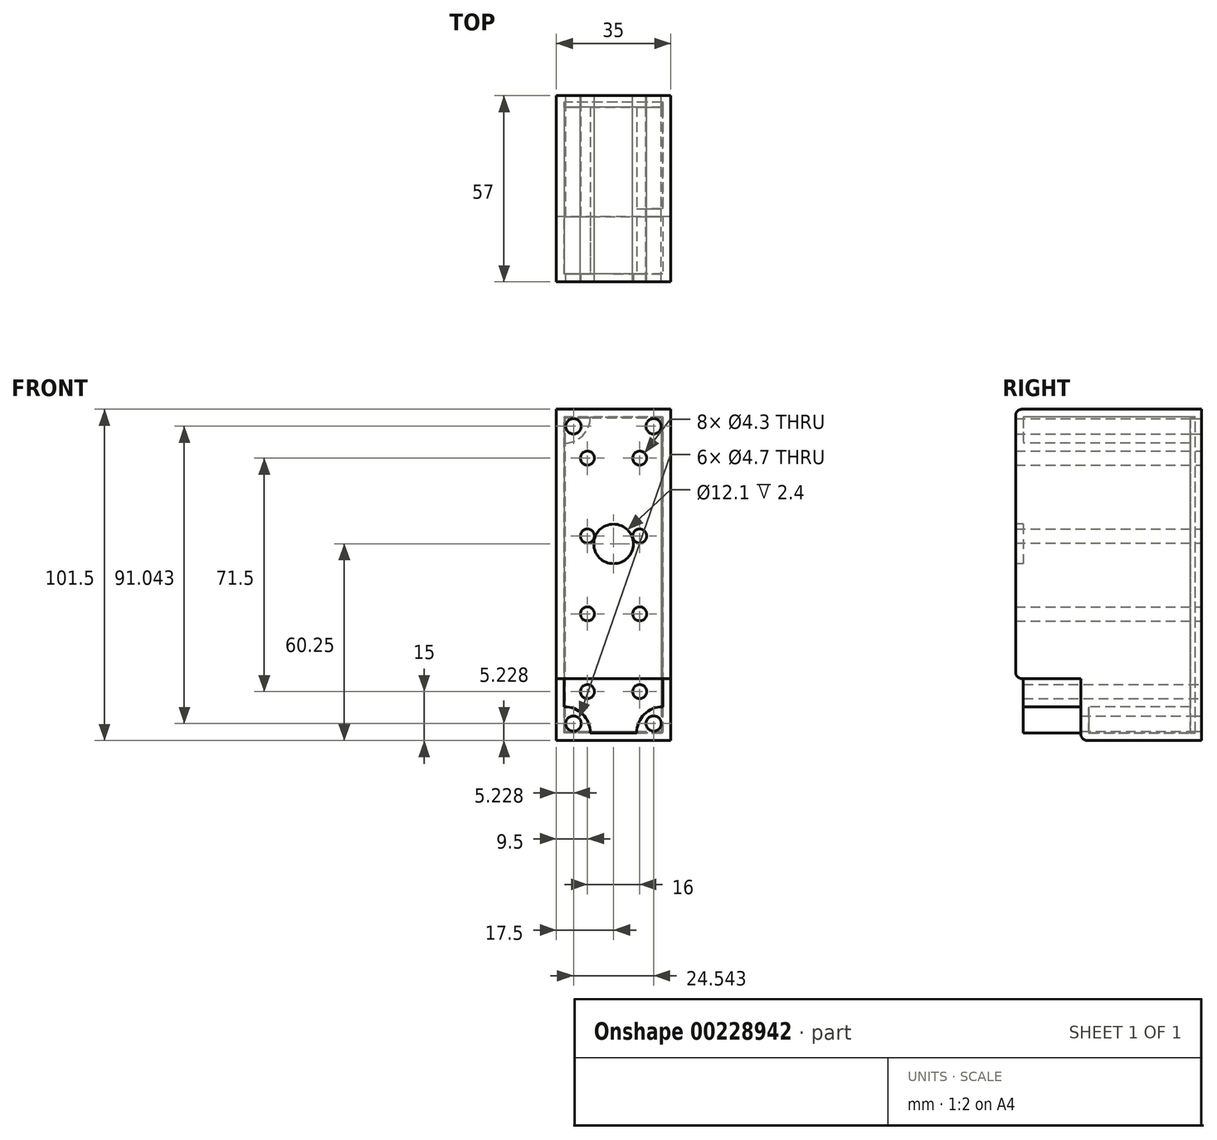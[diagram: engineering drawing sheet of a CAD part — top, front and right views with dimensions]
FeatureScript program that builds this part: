
annotation { "Feature Type Name" : "Feature", "Feature Type Description" : "" }
export const myFeature = defineFeature(function(context is Context, id is Id, definition is map)
    precondition{}
    {
        {
            var Q0;
            Q0=qCreatedBy(makeId("Right.planeOp"),FACE);
            var sketch = newSketch(context, id + "F0", { "sketchPlane" : qUnion([Q0])});
            skLineSegment(sketch, "E0", {"start": v(20, 0) * mm, "end": v(55, 0) * mm});
            skLineSegment(sketch, "E1", {"start": v(55, 0) * mm, "end": v(55, 101.5) * mm});
            skLineSegment(sketch, "E2", {"start": v(55, 101.5) * mm, "end": v(0, 101.5) * mm});
            skLineSegment(sketch, "E3", {"start": v(0, 101.5) * mm, "end": v(0, 19) * mm});
            skLineSegment(sketch, "E4", {"start": v(0, 19) * mm, "end": v(20, 19) * mm});
            skLineSegment(sketch, "E5", {"start": v(20, 19) * mm, "end": v(20, 0) * mm});
            skSolve(sketch);
        }
        {
            var Q0;
            Q0=makeQuery(id+"F0.imprint","IMPRINT",FACE,{"disambiguationData":[TD([[makeQuery(id+"F0.imprint","IMPRINT",EDGE,{"derivedFrom":sQuery(id+"F0.wireOp",EDGE,"E0")}),1.0]])]});
            extrude(context, id + "F1", {"entities" : qUnion([Q0]), "depth" : 35 * mm});
        }
        {
            var Q0;
            Q0=makeQuery(id+"F1.opExtrude","SWEPT_EDGE",EDGE,{"disambiguationData":[OSD([sQuery(id+"F0.wireOp",EDGE,"E2"),sQuery(id+"F0.wireOp",EDGE,"E3")])]});
            var Q1;
            Q1=makeQuery(id+"F1.opExtrude","SWEPT_EDGE",EDGE,{"disambiguationData":[OSD([sQuery(id+"F0.wireOp",EDGE,"E3"),sQuery(id+"F0.wireOp",EDGE,"E4")])]});
            var Q2;
            Q2=makeQuery(id+"F1.opExtrude","SWEPT_EDGE",EDGE,{"disambiguationData":[OSD([sQuery(id+"F0.wireOp",EDGE,"E0"),sQuery(id+"F0.wireOp",EDGE,"E5")])]});
            fillet(context, id + "F2", {"entities" : qUnion([Q0, Q1, Q2]), "radius" : 2 * mm, "tangentPropagation" : true, "allowEdgeOverflow" : false});
        }
        {
            var Q0;
            Q0=makeQuery(id+"F1.opExtrude","SWEPT_FACE",FACE,{"disambiguationData":[OSD([sQuery(id+"F0.wireOp",EDGE,"E1")])]});
            shell(context, id + "F3", {"entities" : qUnion([Q0]), "thickness" : 2.4 * mm});
        }
        {
            var Q0;
            Q0=makeQuery(id+"F1.opExtrude","SWEPT_FACE",FACE,{"disambiguationData":[OSD([sQuery(id+"F0.wireOp",EDGE,"E3")])]});
            var sketch = newSketch(context, id + "F4", { "sketchPlane" : qUnion([Q0])});
            skPoint(sketch, "E6.0", {"position": v(0, 101.5) * mm});
            skPoint(sketch, "E7.0", {"position": v(35, 19) * mm});
            skLineSegment(sketch, "E8", {"start": v(0, 101.5) * mm, "end": v(35, 19) * mm, "construction": true});
            skCircle(sketch, "E9", {"center": v(17.5, 60.25) * mm, "radius": 6.05 * mm});
            skSolve(sketch);
        }
        {
            var Q0;
            Q0=makeQuery(id+"F4.imprint","IMPRINT",FACE,{"disambiguationData":[TD([[makeQuery(id+"F4.imprint","IMPRINT",EDGE,{"derivedFrom":sQuery(id+"F4.wireOp",EDGE,"E9")}),1.0]])]});
            extrude(context, id + "F5", {"entities" : qUnion([Q0]), "operationType" : NewBodyOperationType.REMOVE, "endBound" : BoundingType.THROUGH_ALL, "oppositeDirection" : true, "depth" : 25 * mm});
        }
        {
            var Q0;
            Q0=makeQuery(id+"F1.opExtrude","SWEPT_FACE",FACE,{"disambiguationData":[OSD([sQuery(id+"F0.wireOp",EDGE,"E1")])]});
            var sketch = newSketch(context, id + "F6", { "sketchPlane" : qUnion([Q0])});
            skLineSegment(sketch, "E10.0", {"start": v(-35, 101.5) * mm, "end": v(0, 101.5) * mm});
            skLineSegment(sketch, "E11.0", {"start": v(-35, 0) * mm, "end": v(-35, 101.5) * mm});
            skLineSegment(sketch, "E12.0", {"start": v(-35, 0) * mm, "end": v(0, 0) * mm});
            skLineSegment(sketch, "E13.0", {"start": v(0, 0) * mm, "end": v(0, 101.5) * mm});
            skLineSegment(sketch, "E14.0", {"start": v(-32.25, 98.75) * mm, "end": v(-2.75, 98.75) * mm});
            skLineSegment(sketch, "E14.1", {"start": v(-32.25, 2.75) * mm, "end": v(-32.25, 98.75) * mm});
            skLineSegment(sketch, "E14.2", {"start": v(-32.25, 2.75) * mm, "end": v(-2.75, 2.75) * mm});
            skLineSegment(sketch, "E14.3", {"start": v(-2.75, 2.75) * mm, "end": v(-2.75, 98.75) * mm});
            skSolve(sketch);
        }
        {
            var Q0;
            Q0=makeQuery(id+"F6.imprint","IMPRINT",FACE,{"disambiguationData":[TD([[makeQuery(id+"F6.imprint","IMPRINT",EDGE,{"derivedFrom":sQuery(id+"F6.wireOp",EDGE,"E14.0")}),-1.0]])]});
            extrude(context, id + "F7", {"entities" : qUnion([Q0]), "oppositeDirection" : true, "depth" : 1.5 * mm});
        }
        {
            var Q0;
            Q0=makeQuery(id+"F6.imprint","IMPRINT",FACE,{"disambiguationData":[TD([[makeQuery(id+"F6.imprint","IMPRINT",EDGE,{"derivedFrom":sQuery(id+"F6.wireOp",EDGE,"E10.0")}),-1.0]])]});
            var Q1;
            Q1=makeQuery(id+"F6.imprint","IMPRINT",FACE,{"disambiguationData":[TD([[makeQuery(id+"F6.imprint","IMPRINT",EDGE,{"derivedFrom":sQuery(id+"F6.wireOp",EDGE,"E14.0")}),-1.0]])]});
            var Q2;
            Q2=makeQuery(id+"F6.imprint","IMPRINT",FACE,{"disambiguationData":[TD([[makeQuery(id+"F6.imprint","IMPRINT",EDGE,{"derivedFrom":sQuery(id+"F6.wireOp",EDGE,"E14.0")}),1.0]])]});
            extrude(context, id + "F8", {"entities" : qUnion([Q0, Q1, Q2]), "operationType" : NewBodyOperationType.ADD, "depth" : 2 * mm});
        }
        {
            var Q0;
            Q0=makeQuery(id+"F3.opShell","OFFSET_FACE",FACE,{"disambiguationData":[OSD([sQuery(id+"F0.wireOp",EDGE,"E3")])]});
            var sketch = newSketch(context, id + "F9", { "sketchPlane" : qUnion([Q0])});
            skLineSegment(sketch, "E15.0", {"start": v(-32.6, 99.1) * mm, "end": v(-2.4, 99.1) * mm});
            skLineSegment(sketch, "E16.0", {"start": v(-32.6, 2.4) * mm, "end": v(-32.6, 99.1) * mm});
            skLineSegment(sketch, "E17.0", {"start": v(-32.6, 2.4) * mm, "end": v(-2.4, 2.4) * mm});
            skLineSegment(sketch, "E18.0", {"start": v(-2.4, 2.4) * mm, "end": v(-2.4, 99.1) * mm});
            skArc(sketch, "E19", {"start": v(-32.6, 91.1) * mm, "mid": v(-26.94, 93.44) * mm, "end": v(-24.6, 99.1) * mm});
            skCircle(sketch, "E20", {"center": v(-29.77, 96.27) * mm, "radius": 1.75 * mm});
            skLineSegment(sketch, "E21", {"start": v(-32.6, 99.1) * mm, "end": v(-26.94, 93.44) * mm, "construction": true});
            skLineSegment(sketch, "E22", {"start": v(-17.5, 99.1) * mm, "end": v(-17.5, 2.4) * mm, "construction": true});
            skLineSegment(sketch, "E23", {"start": v(-32.6, 50.75) * mm, "end": v(-2.4, 50.75) * mm, "construction": true});
            skArc(sketch, "E24.MirrorCS", {"start": v(-2.4, 91.1) * mm, "mid": v(-8.06, 93.44) * mm, "end": v(-10.4, 99.1) * mm});
            skCircle(sketch, "E25.MirrorC", {"center": v(-5.23, 96.27) * mm, "radius": 1.75 * mm});
            skArc(sketch, "E26.MirrorCS", {"start": v(-32.6, 10.4) * mm, "mid": v(-26.94, 8.06) * mm, "end": v(-24.6, 2.4) * mm});
            skCircle(sketch, "E27.MirrorC", {"center": v(-29.77, 5.23) * mm, "radius": 1.75 * mm});
            skArc(sketch, "E28.MirrorCS", {"start": v(-2.4, 10.4) * mm, "mid": v(-8.06, 8.06) * mm, "end": v(-10.4, 2.4) * mm});
            skCircle(sketch, "E29.MirrorC", {"center": v(-5.23, 5.23) * mm, "radius": 1.75 * mm});
            skSolve(sketch);
        }
        {
            var Q0;
            {var subQ3=sQuery(id+"F9.wireOp",EDGE,"E24.MirrorCS");Q0=makeQuery(id+"F9.imprint","IMPRINT",FACE,{"disambiguationData":[TD([[makeQuery(id+"F9.imprint","IMPRINT",EDGE,{"derivedFrom":subQ3}),-1.0]])]});}
            var Q1;
            {var subQ3=sQuery(id+"F9.wireOp",EDGE,"E19");Q1=makeQuery(id+"F9.imprint","IMPRINT",FACE,{"disambiguationData":[TD([[makeQuery(id+"F9.imprint","IMPRINT",EDGE,{"derivedFrom":subQ3}),1.0]])]});}
            var Q2;
            Q2=makeQuery(id+"F7.opExtrude","CAP_FACE",FACE,{"disambiguationData":[OSD([sQuery(id+"F6.wireOp",EDGE,"E14.0"),sQuery(id+"F6.wireOp",EDGE,"E14.1"),sQuery(id+"F6.wireOp",EDGE,"E14.2"),sQuery(id+"F6.wireOp",EDGE,"E14.3")])],"isStart":false});
            extrude(context, id + "F10", {"entities" : qUnion([Q0, Q1]), "operationType" : NewBodyOperationType.ADD, "endBound" : BoundingType.UP_TO_SURFACE, "endBoundEntityFace" : qUnion([Q2]), "depth" : 25 * mm});
        }
        {
            var Q0;
            {var subQ3=sQuery(id+"F9.wireOp",EDGE,"E26.MirrorCS");Q0=makeQuery(id+"F9.imprint","IMPRINT",FACE,{"disambiguationData":[TD([[makeQuery(id+"F9.imprint","IMPRINT",EDGE,{"derivedFrom":subQ3}),-1.0]])]});}
            var Q1;
            {var subQ3=sQuery(id+"F9.wireOp",EDGE,"E28.MirrorCS");Q1=makeQuery(id+"F9.imprint","IMPRINT",FACE,{"disambiguationData":[TD([[makeQuery(id+"F9.imprint","IMPRINT",EDGE,{"derivedFrom":subQ3}),1.0]])]});}
            var Q2;
            Q2=makeQuery(id+"F7.opExtrude","CAP_FACE",FACE,{"disambiguationData":[OSD([sQuery(id+"F6.wireOp",EDGE,"E14.0"),sQuery(id+"F6.wireOp",EDGE,"E14.1"),sQuery(id+"F6.wireOp",EDGE,"E14.2"),sQuery(id+"F6.wireOp",EDGE,"E14.3")])],"isStart":false});
            var Q3;
            Q3=makeQuery(id+"F1.opExtrude","SWEPT_FACE",FACE,{"disambiguationData":[OSD([sQuery(id+"F0.wireOp",EDGE,"E5")])]});
            extrude(context, id + "F11", {"entities" : qUnion([Q0, Q1]), "operationType" : NewBodyOperationType.ADD, "endBound" : BoundingType.UP_TO_SURFACE, "endBoundEntityFace" : qUnion([Q2]), "depth" : 25 * mm, "hasSecondDirection" : true, "secondDirectionBound" : SecondDirectionBoundingType.UP_TO_SURFACE, "secondDirectionOppositeDirection" : false, "secondDirectionBoundEntityFace" : qUnion([Q3]), "secondDirectionDepth" : 13 * mm});
        }
        {
            var Q0;
            Q0=makeQuery(id+"F8.opExtrude","CAP_FACE",FACE,{"disambiguationData":[OSD([sQuery(id+"F6.wireOp",EDGE,"E10.0"),sQuery(id+"F6.wireOp",EDGE,"E11.0"),sQuery(id+"F6.wireOp",EDGE,"E12.0"),sQuery(id+"F6.wireOp",EDGE,"E13.0")])],"isStart":false});
            var sketch = newSketch(context, id + "F12", { "sketchPlane" : qUnion([Q0])});
            skCircle(sketch, "E30.0", {"center": v(-5.23, 96.27) * mm, "radius": 2.35 * mm});
            skCircle(sketch, "E31.0", {"center": v(-29.77, 96.27) * mm, "radius": 2.35 * mm});
            skCircle(sketch, "E32.0", {"center": v(-29.77, 5.23) * mm, "radius": 2.35 * mm});
            skCircle(sketch, "E33.0", {"center": v(-5.23, 5.23) * mm, "radius": 2.35 * mm});
            skSolve(sketch);
        }
        {
            var Q0;
            Q0 = qSketchRegion(id + "F12", true);
            extrude(context, id + "F13", {"entities" : qUnion([Q0]), "operationType" : NewBodyOperationType.REMOVE, "endBound" : BoundingType.THROUGH_ALL, "oppositeDirection" : true, "depth" : 25 * mm});
        }
        {
            var Q0;
            Q0=makeQuery(id+"F8.opExtrude","CAP_FACE",FACE,{"disambiguationData":[OSD([sQuery(id+"F6.wireOp",EDGE,"E10.0"),sQuery(id+"F6.wireOp",EDGE,"E11.0"),sQuery(id+"F6.wireOp",EDGE,"E12.0"),sQuery(id+"F6.wireOp",EDGE,"E13.0")])],"isStart":false});
            var sketch = newSketch(context, id + "F14", { "sketchPlane" : qUnion([Q0])});
            skLineSegment(sketch, "E34", {"start": v(-17.5, 101.5) * mm, "end": v(-17.5, 0) * mm, "construction": true});
            skCircle(sketch, "E35", {"center": v(-25.5, 86.5) * mm, "radius": 2.15 * mm});
            skCircle(sketch, "E36", {"center": v(-9.5, 86.5) * mm, "radius": 2.15 * mm});
            skCircle(sketch, "E37", {"center": v(-25.5, 86.5) * mm, "radius": 6.1 * mm, "construction": true});
            skCircle(sketch, "E38", {"center": v(-9.5, 86.5) * mm, "radius": 6.1 * mm, "construction": true});
            skLineSegment(sketch, "E39", {"start": v(-9.5, 86.5) * mm, "end": v(-25.5, 86.5) * mm, "construction": true});
            skCircle(sketch, "E40.0.1.0", {"center": v(-25.5, 62.67) * mm, "radius": 2.15 * mm});
            skCircle(sketch, "E40.0.1.1", {"center": v(-25.5, 62.67) * mm, "radius": 6.1 * mm, "construction": true});
            skCircle(sketch, "E40.0.1.2", {"center": v(-9.5, 62.67) * mm, "radius": 2.15 * mm});
            skCircle(sketch, "E40.0.1.3", {"center": v(-9.5, 62.67) * mm, "radius": 6.1 * mm, "construction": true});
            skCircle(sketch, "E40.0.2.0", {"center": v(-25.5, 38.83) * mm, "radius": 2.15 * mm});
            skCircle(sketch, "E40.0.2.1", {"center": v(-25.5, 38.83) * mm, "radius": 6.1 * mm, "construction": true});
            skCircle(sketch, "E40.0.2.2", {"center": v(-9.5, 38.83) * mm, "radius": 2.15 * mm});
            skCircle(sketch, "E40.0.2.3", {"center": v(-9.5, 38.83) * mm, "radius": 6.1 * mm, "construction": true});
            skCircle(sketch, "E40.0.3.0", {"center": v(-25.5, 15) * mm, "radius": 2.15 * mm});
            skCircle(sketch, "E40.0.3.1", {"center": v(-25.5, 15) * mm, "radius": 6.1 * mm, "construction": true});
            skCircle(sketch, "E40.0.3.2", {"center": v(-9.5, 15) * mm, "radius": 2.15 * mm});
            skCircle(sketch, "E40.0.3.3", {"center": v(-9.5, 15) * mm, "radius": 6.1 * mm, "construction": true});
            skLineSegment(sketch, "E40.direction1", {"start": v(-25.5, 86.5) * mm, "end": v(-9.5, 86.5) * mm, "construction": true});
            skLineSegment(sketch, "E40.direction2", {"start": v(-25.5, 86.5) * mm, "end": v(-25.5, 62.67) * mm, "construction": true});
            skLineSegment(sketch, "E41", {"start": v(-25.5, 86.5) * mm, "end": v(-29.77, 96.27) * mm, "construction": true});
            skLineSegment(sketch, "E42", {"start": v(-25.5, 15) * mm, "end": v(-29.77, 5.23) * mm, "construction": true});
            skSolve(sketch);
        }
        {
            var Q0;
            Q0 = qSketchRegion(id + "F14", true);
            extrude(context, id + "F15", {"entities" : qUnion([Q0]), "operationType" : NewBodyOperationType.REMOVE, "endBound" : BoundingType.THROUGH_ALL, "oppositeDirection" : true, "depth" : 25 * mm});
        }
    });
